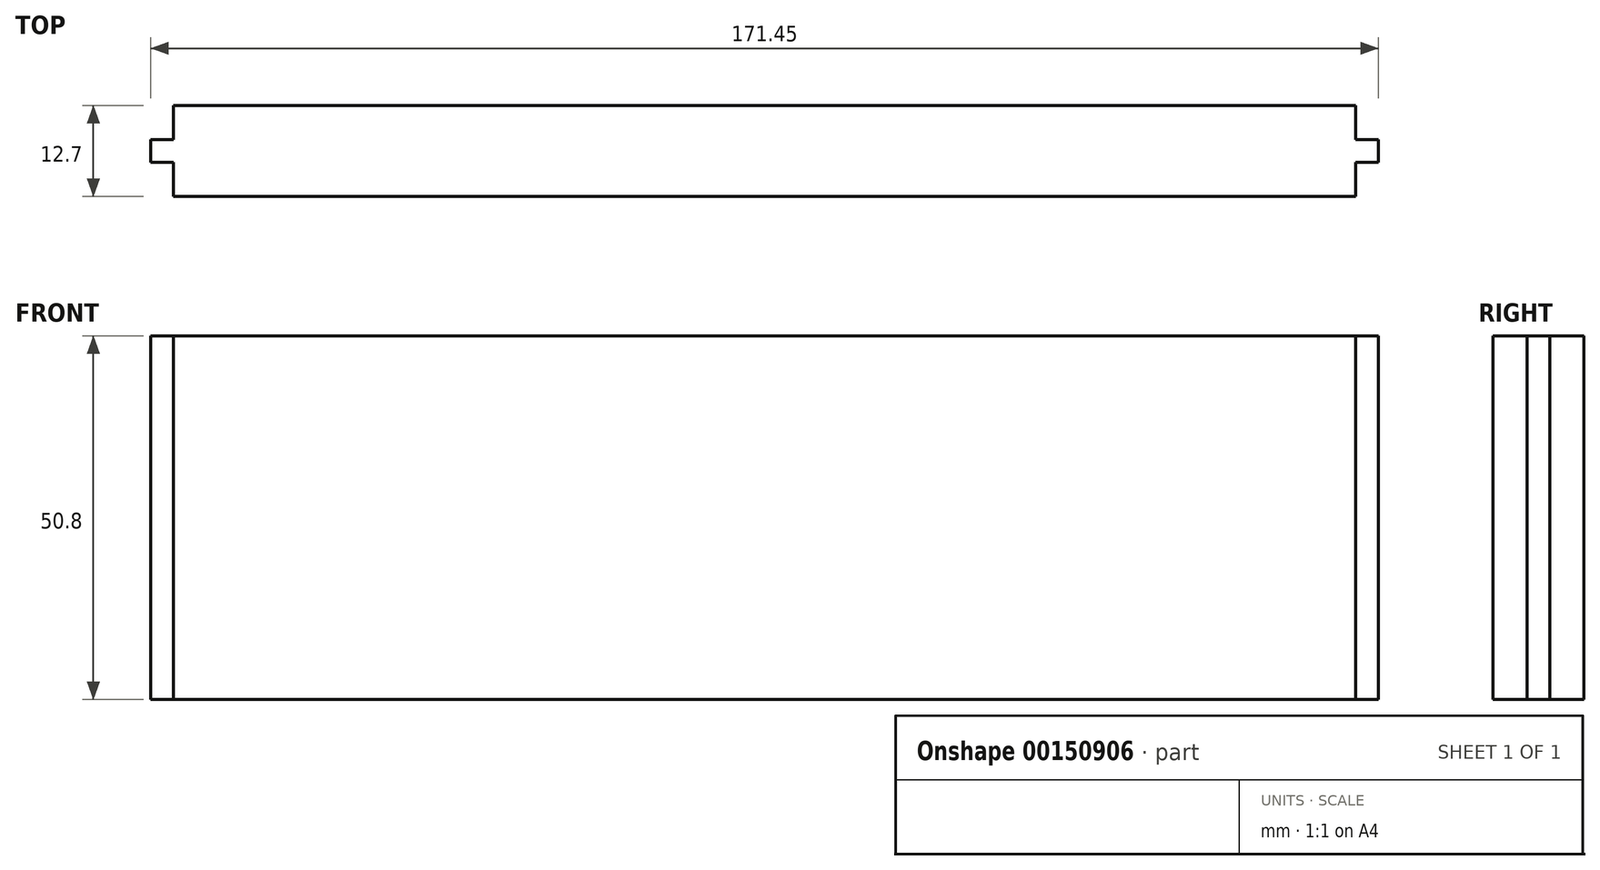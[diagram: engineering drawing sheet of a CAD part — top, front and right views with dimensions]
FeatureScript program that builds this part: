
annotation { "Feature Type Name" : "Feature", "Feature Type Description" : "" }
export const myFeature = defineFeature(function(context is Context, id is Id, definition is map)
    precondition{}
    {
        {
            var Q0;
            Q0=qCreatedBy(makeId("Top.planeOp"),FACE);
            var sketch = newSketch(context, id + "F0", { "sketchPlane" : qUnion([Q0])});
            skLineSegment(sketch, "E0.bottom", {"start": v(-86.18, -6.27) * mm, "end": v(78.92, -6.27) * mm});
            skLineSegment(sketch, "E0.top", {"start": v(-86.18, -18.97) * mm, "end": v(78.92, -18.97) * mm});
            skLineSegment(sketch, "E0.left", {"start": v(-86.18, -6.27) * mm, "end": v(-86.18, -11.03) * mm});
            skLineSegment(sketch, "E0.right", {"start": v(78.92, -6.27) * mm, "end": v(78.92, -11.03) * mm});
            skLineSegment(sketch, "E1.bottom", {"start": v(-89.36, -11.03) * mm, "end": v(-86.18, -11.03) * mm});
            skLineSegment(sketch, "E1.top", {"start": v(-89.36, -14.2) * mm, "end": v(-86.18, -14.2) * mm});
            skLineSegment(sketch, "E1.left", {"start": v(-89.36, -11.03) * mm, "end": v(-89.36, -14.2) * mm});
            skLineSegment(sketch, "E2.bottom", {"start": v(82.1, -11.03) * mm, "end": v(78.92, -11.03) * mm});
            skLineSegment(sketch, "E2.top", {"start": v(82.1, -14.2) * mm, "end": v(78.92, -14.2) * mm});
            skLineSegment(sketch, "E2.left", {"start": v(82.1, -11.03) * mm, "end": v(82.1, -14.2) * mm});
            skLineSegment(sketch, "E3.trimOffspring", {"start": v(-86.18, -14.2) * mm, "end": v(-86.18, -18.97) * mm});
            skLineSegment(sketch, "E4.trimOffspring", {"start": v(78.92, -14.2) * mm, "end": v(78.92, -18.97) * mm});
            skSolve(sketch);
        }
        {
            var Q0;
            Q0 = qSketchRegion(id + "F0", true);
            extrude(context, id + "F1", {"entities" : qUnion([Q0]), "depth" : 50.8 * mm});
        }
    });
